# Revit family: PROOX Sanitary napkin disposal bin EN
name_source: partatom
category: Furniture
revit_build: Autodesk Revit 2014 (Build: 20130308_1515(x64)
units: mm (PartAtom-declared; Revit-internal decimal feet)

## types (2) — shared parameters
BIM objects producer = www.BIMtelligent.eu
Manufacturer = PROOX Ltd.
URL = http://www.proox.com

## per-type parameters (varying)
| type | Cost | Description | EAN-Nummer | Material | Model | Specification |
| ONE pure | 215 $ | sanitary napkin disposal bin with integrated bag dispenser PROOX ONE pure made from stainless steel | 9120050350120 | PROOX Stainless steel, brushed | PU-400 | Sanitary napkin disposal bin with integrated bag dispenser. Made out of stainless steel. Surface with fine brushed structure. Cover 1.5 mm thickness. Intended for wall mounting. Perforated designed area with 4mm drillings. Including plastic bin for easy cleaning. 4 litres capacity. Self-closing mechanism. Integrated hygiene bag dispenser for hygiene bag boxes up to 132x87x20mm. Including anchors, stainless steel screws and cover to close the dispenser opening (if bag supply is not offered). |
| ONE dark passion | 245 $ | sanitary napkin disposal bin with integrated bag dispenser PROOX ONE dark passion made from aluminum black anodized | 9120050350243 | PROOX Aluminum, black anodised | DP-400 | Sanitary napkin disposal bin with integrated bag dispenser made out from glass pearl blasted and black anodised aluminum. Cover 3 mm thickness. Intended for wall mounting. Perforated designed area with 4mm drillings. Including plastic bin for easy cleaning. 4 litres capacity. Self-closing mechanism. Integrated hygiene bag dispenser for hygiene bag boxes up to 132x87x20mm. Including anchors, stainless steel screws and cover to close the dispenser opening (if bag supply is not offered). |

note: column(s) folded — value = type name in every type: Type Comments

## geometry (parser evidence)
native form markers: Sweep x1
no freeform markers — native parametric forms only
